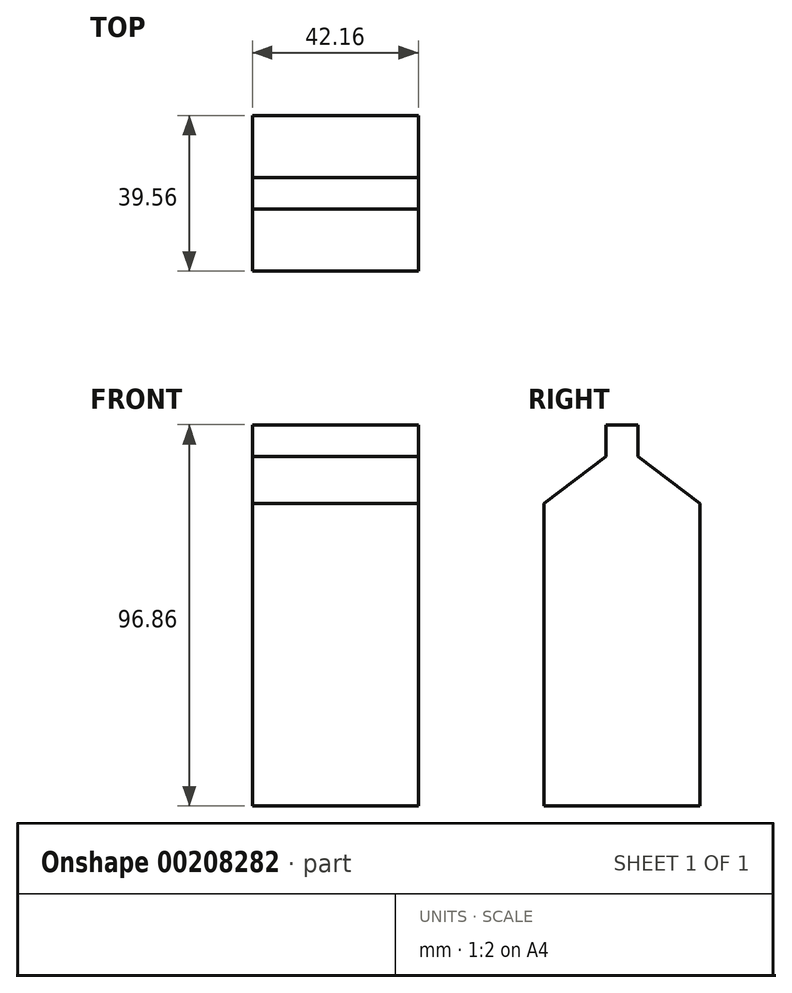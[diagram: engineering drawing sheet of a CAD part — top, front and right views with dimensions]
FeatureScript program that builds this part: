
annotation { "Feature Type Name" : "Feature", "Feature Type Description" : "" }
export const myFeature = defineFeature(function(context is Context, id is Id, definition is map)
    precondition{}
    {
        {
            var Q0;
            Q0=qCreatedBy(makeId("Right.planeOp"),FACE);
            var sketch = newSketch(context, id + "F0", { "sketchPlane" : qUnion([Q0])});
            skLineSegment(sketch, "E0.bottom", {"start": v(19.78, -38.44) * mm, "end": v(-19.78, -38.44) * mm});
            skLineSegment(sketch, "E0.left", {"start": v(19.78, -38.44) * mm, "end": v(19.78, 38.44) * mm});
            skLineSegment(sketch, "E0.right", {"start": v(-19.78, -38.44) * mm, "end": v(-19.78, 38.44) * mm});
            skPoint(sketch, "E0.middle", {"position": v(0, 0) * mm});
            skLineSegment(sketch, "E1", {"start": v(19.78, 38.44) * mm, "end": v(4.04, 50.35) * mm});
            skLineSegment(sketch, "E2", {"start": v(4.04, 50.35) * mm, "end": v(4.04, 58.42) * mm});
            skLineSegment(sketch, "E3", {"start": v(4.04, 58.42) * mm, "end": v(0, 58.42) * mm});
            skLineSegment(sketch, "E4.MirrorCS", {"start": v(-4.04, 58.42) * mm, "end": v(0, 58.42) * mm});
            skLineSegment(sketch, "E5.MirrorCS", {"start": v(-4.04, 50.35) * mm, "end": v(-4.04, 58.42) * mm});
            skLineSegment(sketch, "E6.MirrorCS", {"start": v(-19.78, 38.44) * mm, "end": v(-4.04, 50.35) * mm});
            skSolve(sketch);
        }
        {
            var Q0;
            Q0=makeQuery(id+"F0.imprint","IMPRINT",FACE,{"disambiguationData":[TD([[makeQuery(id+"F0.imprint","IMPRINT",EDGE,{"derivedFrom":sQuery(id+"F0.wireOp",EDGE,"E0.bottom")}),-1.0]])]});
            extrude(context, id + "F1", {"entities" : qUnion([Q0]), "endBound" : BoundingType.SYMMETRIC, "oppositeDirection" : true, "depth" : 42.16 * mm});
        }
    });
